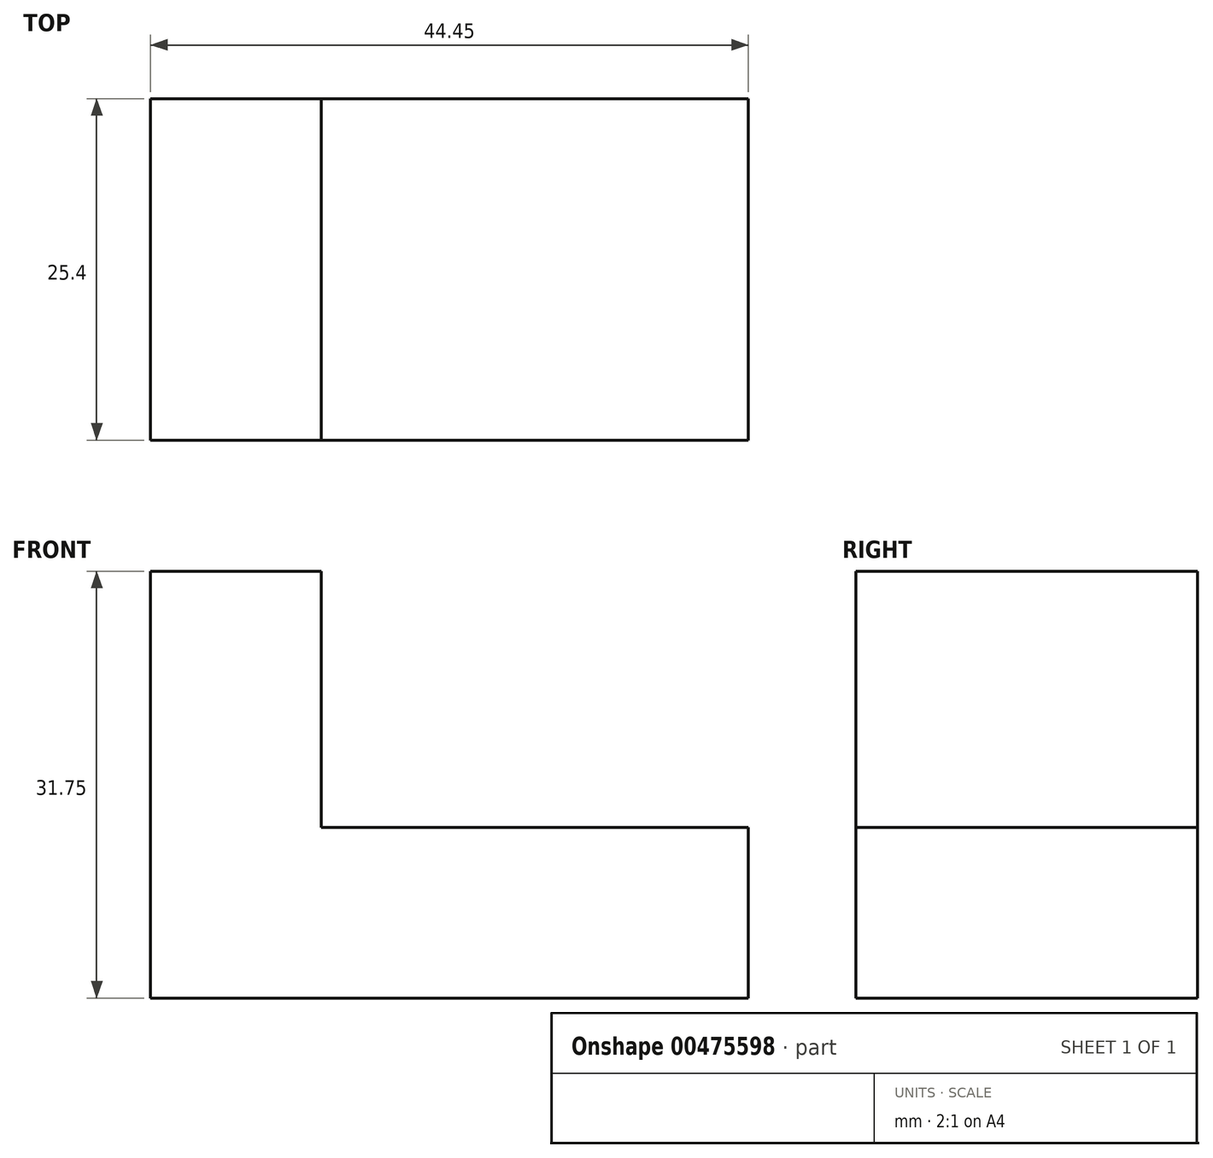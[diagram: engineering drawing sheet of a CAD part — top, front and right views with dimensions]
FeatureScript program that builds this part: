
annotation { "Feature Type Name" : "Feature", "Feature Type Description" : "" }
export const myFeature = defineFeature(function(context is Context, id is Id, definition is map)
    precondition{}
    {
        {
            var Q0;
            Q0=qCreatedBy(makeId("Front.planeOp"),FACE);
            var sketch = newSketch(context, id + "F0", { "sketchPlane" : qUnion([Q0])});
            skLineSegment(sketch, "E0", {"start": v(0, 0) * mm, "end": v(0, 31.75) * mm});
            skLineSegment(sketch, "E1", {"start": v(0, 31.75) * mm, "end": v(12.7, 31.75) * mm});
            skLineSegment(sketch, "E2", {"start": v(12.7, 31.75) * mm, "end": v(12.7, 12.7) * mm});
            skLineSegment(sketch, "E3", {"start": v(12.7, 12.7) * mm, "end": v(44.45, 12.7) * mm});
            skLineSegment(sketch, "E4", {"start": v(44.45, 12.7) * mm, "end": v(44.45, 0) * mm});
            skLineSegment(sketch, "E5", {"start": v(44.45, 0) * mm, "end": v(0, 0) * mm});
            skSolve(sketch);
        }
        {
            var Q0;
            Q0=makeQuery(id+"F0.imprint","IMPRINT",FACE,{"disambiguationData":[TD([[makeQuery(id+"F0.imprint","IMPRINT",EDGE,{"derivedFrom":sQuery(id+"F0.wireOp",EDGE,"E0")}),-1.0]])]});
            extrude(context, id + "F1", {"entities" : qUnion([Q0]), "depth" : 25.4 * mm});
        }
        {
            var Q0;
            Q0=makeQuery(id+"F1.opExtrude","SWEPT_FACE",FACE,{"disambiguationData":[OSD([sQuery(id+"F0.wireOp",EDGE,"E4")])]});
            var sketch = newSketch(context, id + "F2", { "sketchPlane" : qUnion([Q0])});
            skPoint(sketch, "E6.startSnap0", {"position": v(-12.7, 12.7) * mm});
            skLineSegment(sketch, "E7", {"start": v(-16.22, 12.7) * mm, "end": v(-16.22, 31.75) * mm});
            skLineSegment(sketch, "E8", {"start": v(-16.22, 31.75) * mm, "end": v(-9.87, 31.75) * mm});
            skLineSegment(sketch, "E9", {"start": v(-9.87, 31.75) * mm, "end": v(-9.87, 12.7) * mm});
            skSolve(sketch);
        }
        {
            var Q0;
            Q0 = qSketchRegion(id + "F2", true);
            var Q1;
            {var subQ0=sQuery(id+"F2.wireOp",EDGE,"E7");Q1=makeQuery(id+"F2.imprint","IMPRINT",FACE,{"disambiguationData":[TD([[makeQuery(id+"F2.imprint","IMPRINT",EDGE,{"derivedFrom":subQ0}),-1.0]])]});}
            extrude(context, id + "F3", {"entities" : qUnion([Q0, Q1]), "operationType" : NewBodyOperationType.REMOVE, "oppositeDirection" : true, "depth" : 25.4 * mm});
        }
    });
